# Revit family: Electronics_Masking-Generators_Biamp_Qt-Patient-Privacy-System_Privacy-Signs
name_source: partatom
category: Communication Devices
units: mm (PartAtom-declared; Revit-internal decimal feet)

## family parameters
Cut with Voids When Loaded = No
Host = Face
Maintain Annotation Orientation = No
OmniClass Number = 23.85.10.00
OmniClass Title = General Information Systems
Part Type = Normal
Room Calculation Point = No
Round Connector Dimension = Use Diameter
Shared = No

## types (2) — shared parameters
Cable Type = 20AWG 2-Conductor Type CMP (Plenum)
Connector Description = Spring-Loaded Push Terminals, 5VDC @ 75mA
Connector Type = Spring-Loaded Push Terminals
Default Elevation = 48 "
Depth = 4 "
Description = QT® Patient Privacy System for Waiting Rooms, Exam Rooms, and Pharmacies
Housing Material = Biamp - Plastic - White
Input Voltage = 5VDC @ 75mA
Manufacturer = Biamp
Number of Connectors = 1
Product Documentation Link = https://downloads.biamp.com
Product Page URL = https://www.biamp.com
Product data url = https://bimobject.com
URL = https://www.biamp.com
Version = 1
Weight = 0.10 lb
Width = 4 "
zero-valued in all types: Height

## type names (no varying parameters)
- Privacy Sign Outside
- Privacy Sign Inside

note: column(s) folded — value = type name in every type: Model

## geometry (parser evidence)
native form markers: Sweep x2
no freeform markers — native parametric forms only
